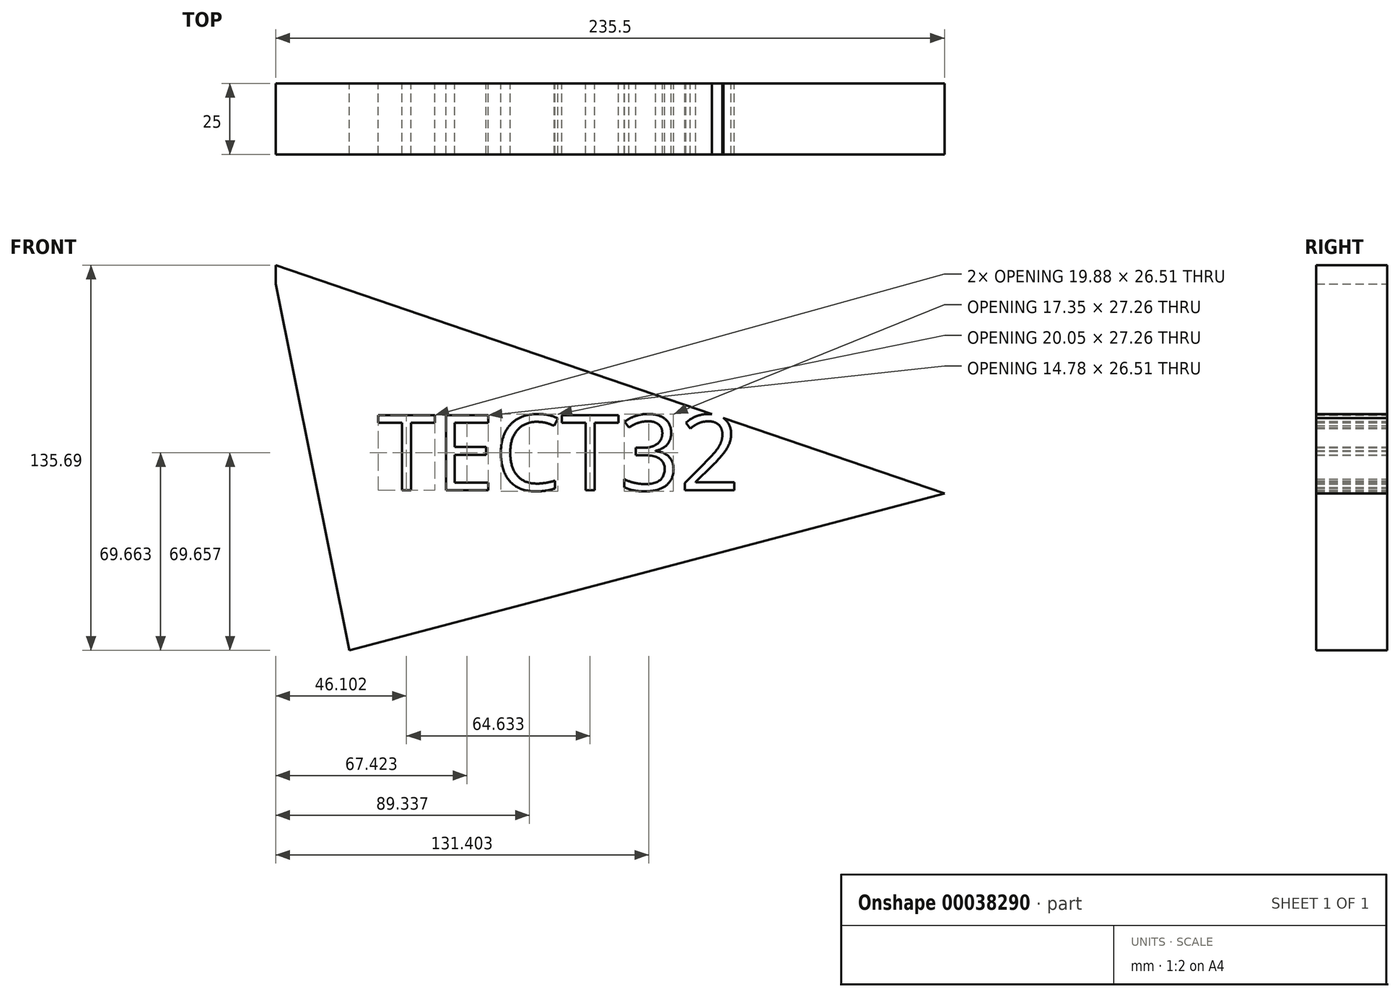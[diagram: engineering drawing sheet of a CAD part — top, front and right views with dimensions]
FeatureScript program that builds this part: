
annotation { "Feature Type Name" : "Feature", "Feature Type Description" : "" }
export const myFeature = defineFeature(function(context is Context, id is Id, definition is map)
    precondition{}
    {
        {
            var Q0;
            Q0=qCreatedBy(makeId("Front.planeOp"),FACE);
            var sketch = newSketch(context, id + "F0", { "sketchPlane" : qUnion([Q0])});
            skLineSegment(sketch, "E0", {"start": v(-126.41, 56.71) * mm, "end": v(109.1, -23.72) * mm});
            skLineSegment(sketch, "E1", {"start": v(109.1, -23.72) * mm, "end": v(-100.43, -78.98) * mm});
            skLineSegment(sketch, "E2", {"start": v(-126.41, 56.71) * mm, "end": v(-126.41, 50.11) * mm});
            skLineSegment(sketch, "E3", {"start": v(-126.41, 50.11) * mm, "end": v(-100.43, -78.98) * mm});
            skText(sketch, "E4", { "text": "ТЕСТ32", "fontName": "OpenSans-Regular.ttf"});
            const initialGuessF0  = {"E4": [-0.09057, -0.02258, 1, 0, 0.02674]};
            skSetInitialGuess(sketch, initialGuessF0);
            skSolve(sketch);
        }
        {
            var Q0;
            Q0=makeQuery(id+"F0.imprint","IMPRINT",FACE,{"disambiguationData":[TD([[makeQuery(id+"F0.imprint","IMPRINT",EDGE,{"derivedFrom":sQuery(id+"F0.wireOp",EDGE,"E0")}),-1.0]])]});
            extrude(context, id + "F1", {"entities" : qUnion([Q0]), "depth" : 25 * mm});
        }
    });
